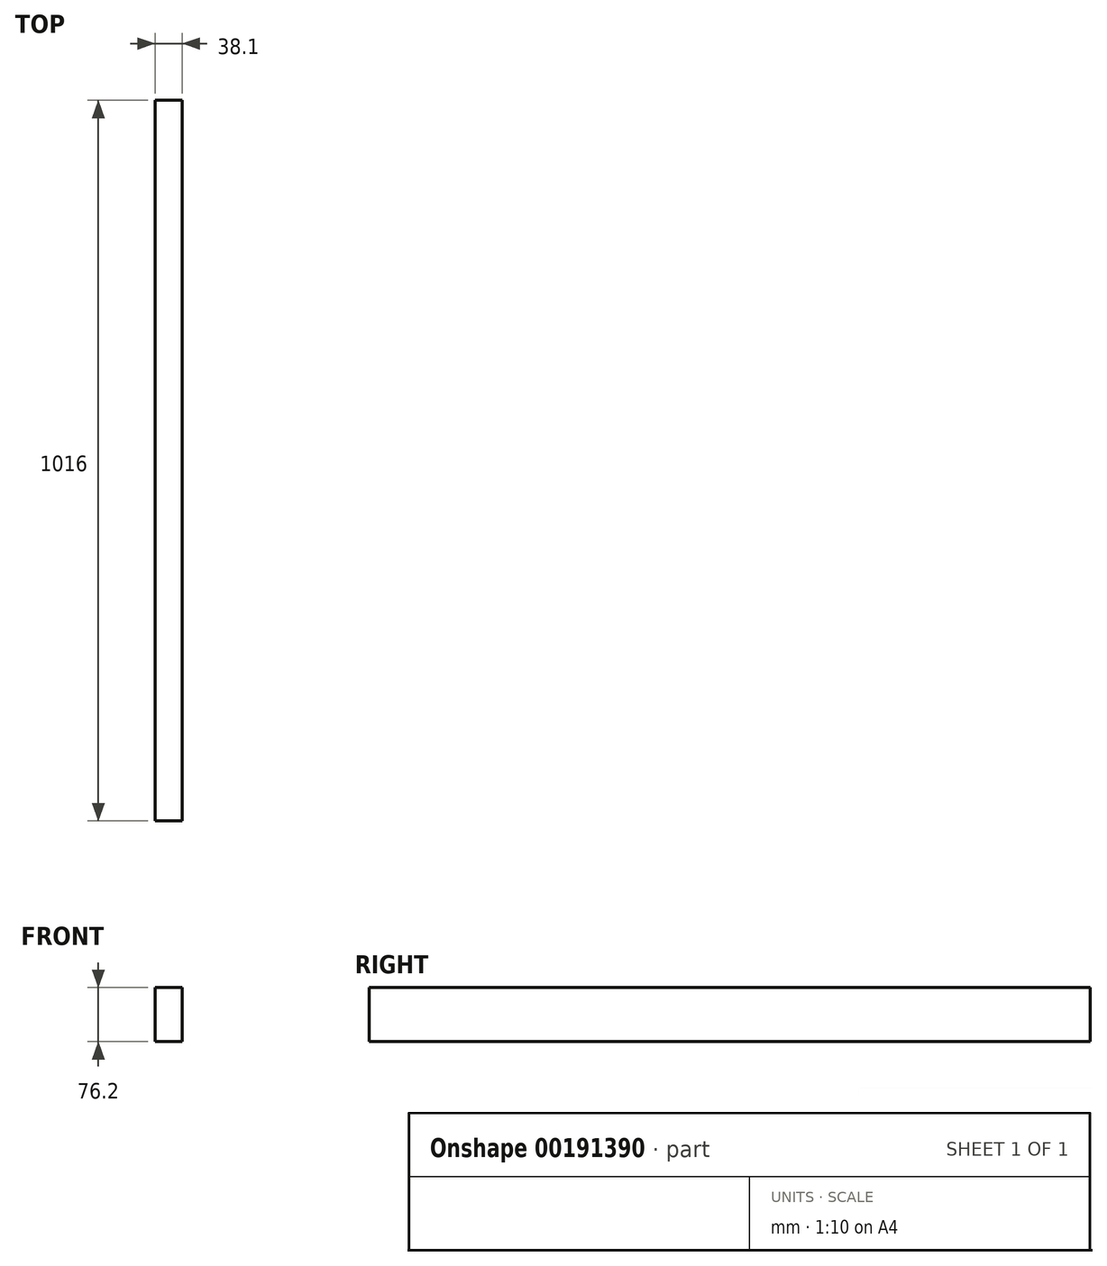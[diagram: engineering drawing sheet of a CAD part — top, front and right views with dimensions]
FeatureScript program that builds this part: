
annotation { "Feature Type Name" : "Feature", "Feature Type Description" : "" }
export const myFeature = defineFeature(function(context is Context, id is Id, definition is map)
    precondition{}
    {
        {
            var Q0;
            Q0=qCreatedBy(makeId("Front.planeOp"),FACE);
            var sketch = newSketch(context, id + "F0", { "sketchPlane" : qUnion([Q0])});
            skLineSegment(sketch, "E0.bottom", {"start": v(-19.05, 38.1) * mm, "end": v(19.05, 38.1) * mm});
            skLineSegment(sketch, "E0.top", {"start": v(-19.05, -38.1) * mm, "end": v(19.05, -38.1) * mm});
            skLineSegment(sketch, "E0.left", {"start": v(-19.05, 38.1) * mm, "end": v(-19.05, -38.1) * mm});
            skLineSegment(sketch, "E0.right", {"start": v(19.05, 38.1) * mm, "end": v(19.05, -38.1) * mm});
            skLineSegment(sketch, "E1", {"start": v(19.05, 38.1) * mm, "end": v(-19.05, -38.1) * mm, "construction": true});
            skSolve(sketch);
        }
        {
            var Q0;
            Q0=makeQuery(id+"F0.imprint","IMPRINT",FACE,{"disambiguationData":[TD([[makeQuery(id+"F0.imprint","IMPRINT",EDGE,{"derivedFrom":sQuery(id+"F0.wireOp",EDGE,"E0.bottom")}),-1.0]])]});
            extrude(context, id + "F1", {"entities" : qUnion([Q0]), "depth" : 1016 * mm});
        }
    });
